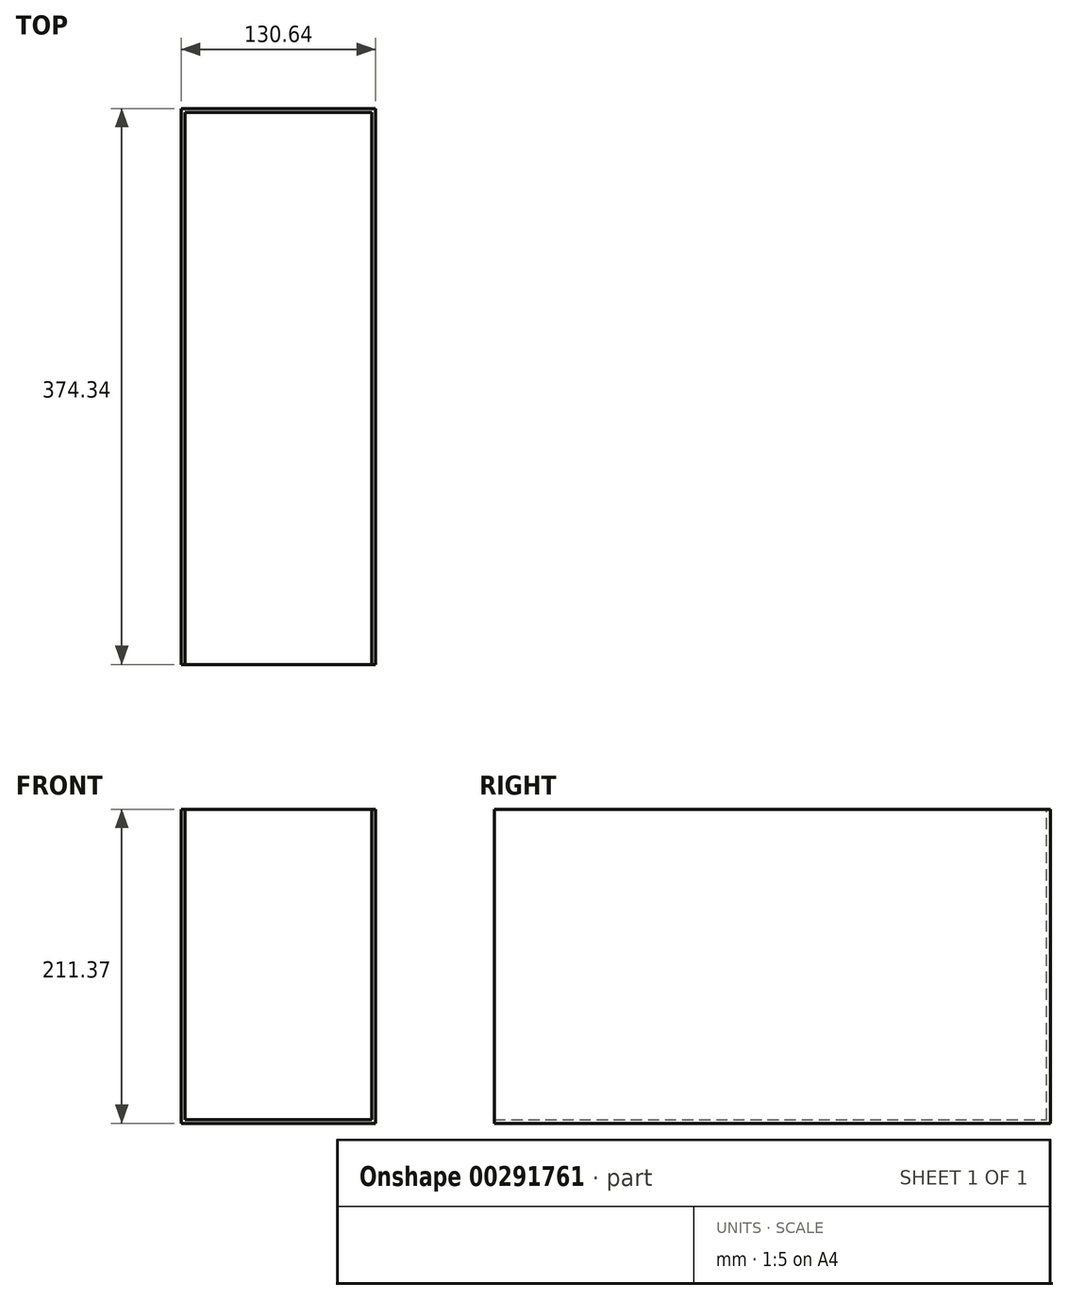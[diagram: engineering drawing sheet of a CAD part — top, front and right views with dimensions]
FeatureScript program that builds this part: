
annotation { "Feature Type Name" : "Feature", "Feature Type Description" : "" }
export const myFeature = defineFeature(function(context is Context, id is Id, definition is map)
    precondition{}
    {
        {
            var Q0;
            Q0=qCreatedBy(makeId("Front.planeOp"),FACE);
            var sketch = newSketch(context, id + "F0", { "sketchPlane" : qUnion([Q0])});
            skLineSegment(sketch, "E0.bottom", {"start": v(0, 0) * mm, "end": v(130.64, 0) * mm});
            skLineSegment(sketch, "E0.top", {"start": v(0, 211.37) * mm, "end": v(130.64, 211.37) * mm});
            skLineSegment(sketch, "E0.left", {"start": v(0, 0) * mm, "end": v(0, 211.37) * mm});
            skLineSegment(sketch, "E0.right", {"start": v(130.64, 0) * mm, "end": v(130.64, 211.37) * mm});
            skSolve(sketch);
        }
        {
            var Q0;
            Q0 = qSketchRegion(id + "F0", true);
            extrude(context, id + "F1", {"entities" : qUnion([Q0]), "depth" : 374.34 * mm});
        }
        {
            var Q0;
            Q0=makeQuery(id+"F1.opExtrude","CAP_FACE",FACE,{"disambiguationData":[OSD([sQuery(id+"F0.wireOp",EDGE,"E0.bottom"),sQuery(id+"F0.wireOp",EDGE,"E0.top"),sQuery(id+"F0.wireOp",EDGE,"E0.left"),sQuery(id+"F0.wireOp",EDGE,"E0.right")])],"isStart":false});
            var Q1;
            Q1=makeQuery(id+"F1.opExtrude","SWEPT_FACE",FACE,{"disambiguationData":[OSD([sQuery(id+"F0.wireOp",EDGE,"E0.top")])]});
            shell(context, id + "F2", {"entities" : qUnion([Q0, Q1]), "thickness" : 2.54 * mm});
        }
    });
